# Revit family: rba-bim-rba4177-series
name_source: partatom
category: Plumbing Fixtures
revit_build: Autodesk Revit 2016 (Build: 20151007_0715(x64)
units: mm (PartAtom-declared; Revit-internal decimal feet)

## family parameters
Always vertical = Yes
Cut with Voids When Loaded = No
Part Type = Normal
Room Calculation Point = No
Round Connector Dimension = Use Diameter
Shared = No
Work Plane-Based = No

## types (3) — shared parameters
Manufacturer = RBA Group
Materials and Finishes = Aluminum
Modified Issue = 20160517.01 $

## per-type parameters (varying)
| type | Description | Length | Model | URL |
| RBA4177-120 | Shower Curtain Track, Aluminium 1200mm x 1200mm | 1200 mm | rba4177-120 | http://www.rba.com.au |
| RBA4177-150 | Shower Curtain Track, Aluminium 1500mm x 1500mm | 1500 mm | RBA4177-150 | www.rba.com.au |
| RBA4177-161 | Shower Curtain Track, Aluminium 1635mm x 1635mm | 1635 mm  [stored 5.36417 ft] | RBA4177-161 | www.rba.com.au |

note: [stored X ft] marks values corroborated as IEEE doubles in the binary element streams (Revit-internal decimal feet)

## geometry (parser evidence)
native form markers: Blend x20, Sweep x3
no freeform markers — native parametric forms only
